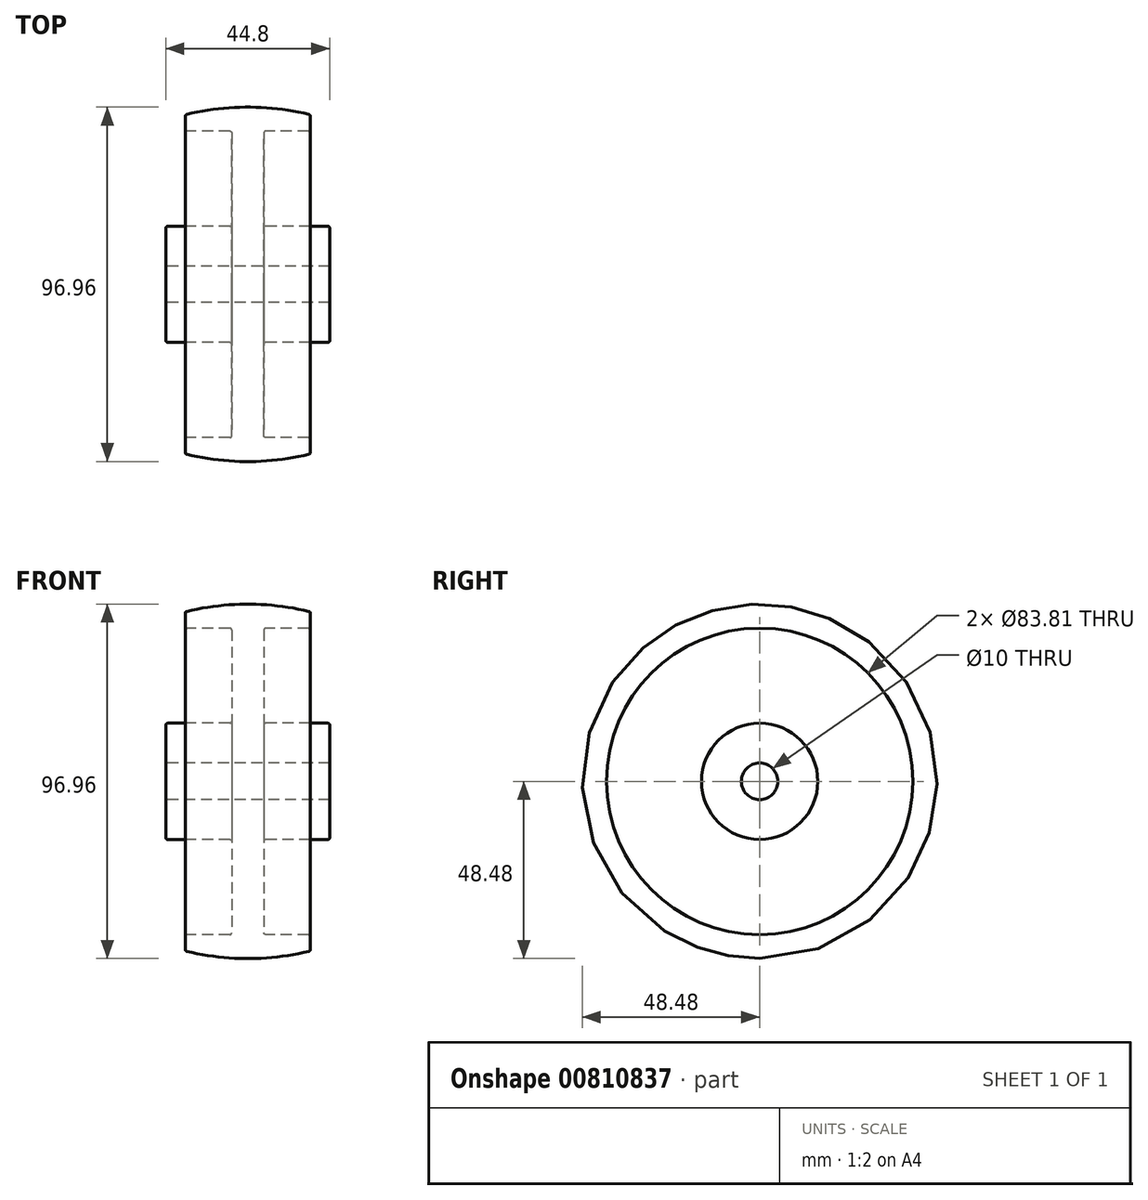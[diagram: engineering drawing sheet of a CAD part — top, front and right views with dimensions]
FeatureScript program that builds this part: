
annotation { "Feature Type Name" : "Feature", "Feature Type Description" : "" }
export const myFeature = defineFeature(function(context is Context, id is Id, definition is map)
    precondition{}
    {
        {
            var Q0;
            Q0=qCreatedBy(makeId("Front.planeOp"),FACE);
            var sketch = newSketch(context, id + "F0", { "sketchPlane" : qUnion([Q0])});
            skLineSegment(sketch, "E0", {"start": v(0, 5) * mm, "end": v(22.4, 5) * mm});
            skLineSegment(sketch, "E1", {"start": v(22.4, 5) * mm, "end": v(22.4, 15.9) * mm});
            skLineSegment(sketch, "E2", {"start": v(22.4, 15.9) * mm, "end": v(4.4, 15.9) * mm});
            skLineSegment(sketch, "E3", {"start": v(4.4, 15.9) * mm, "end": v(4.4, 41.9) * mm});
            skLineSegment(sketch, "E4", {"start": v(4.4, 41.9) * mm, "end": v(17.1, 41.9) * mm});
            skLineSegment(sketch, "E5", {"start": v(17.1, 41.9) * mm, "end": v(17.1, 46.4) * mm});
            skLineSegment(sketch, "E6.MirrorCS", {"start": v(-17.1, 41.9) * mm, "end": v(-17.1, 46.4) * mm});
            skLineSegment(sketch, "E7.MirrorCS", {"start": v(-4.4, 41.9) * mm, "end": v(-17.1, 41.9) * mm});
            skLineSegment(sketch, "E8.MirrorCS", {"start": v(-4.4, 15.9) * mm, "end": v(-4.4, 41.9) * mm});
            skLineSegment(sketch, "E9.MirrorCS", {"start": v(-22.4, 15.9) * mm, "end": v(-4.4, 15.9) * mm});
            skLineSegment(sketch, "E10.MirrorCS", {"start": v(-22.4, 5) * mm, "end": v(-22.4, 15.9) * mm});
            skLineSegment(sketch, "E11.MirrorCS", {"start": v(0, 5) * mm, "end": v(-22.4, 5) * mm});
            skArc(sketch, "E12", {"start": v(17.1, 46.4) * mm, "mid": v(8.6, 47.96) * mm, "end": v(0, 48.48) * mm});
            skArc(sketch, "E13", {"start": v(-17.1, 46.4) * mm, "mid": v(-8.6, 47.96) * mm, "end": v(0, 48.48) * mm});
            skLineSegment(sketch, "E14", {"start": v(-62.65, 0) * mm, "end": v(79.48, 0) * mm});
            skSolve(sketch);
        }
        {
            var Q0;
            Q0=makeQuery(id+"F0.imprint","IMPRINT",FACE,{"disambiguationData":[TD([[makeQuery(id+"F0.imprint","IMPRINT",EDGE,{"derivedFrom":sQuery(id+"F0.wireOp",EDGE,"E0")}),1.0]])]});
            var Q1;
            Q1=sQuery(id+"F0.wireOp",EDGE,"E14");
            revolve(context, id + "F1", {"surfaceOperationType" : NewSurfaceOperationType.NEW, "entities" : qUnion([Q0]), "axis" : qUnion([Q1]), "revolveType" : RevolveType.FULL});
        }
        {
            var Q0;
            Q0=makeQuery(id+"F1.opRevolve","SWEPT_EDGE",EDGE,{"disambiguationData":[OSD([sQuery(id+"F0.wireOp",EDGE,"E6.MirrorCS"),sQuery(id+"F0.wireOp",EDGE,"E13")])]});
            var Q1;
            Q1=makeQuery(id+"F1.opRevolve","SWEPT_EDGE",EDGE,{"disambiguationData":[OSD([sQuery(id+"F0.wireOp",EDGE,"E5"),sQuery(id+"F0.wireOp",EDGE,"E12")])]});
            var Q2;
            Q2=makeQuery(id+"F1.opRevolve","SWEPT_EDGE",EDGE,{"disambiguationData":[OSD([sQuery(id+"F0.wireOp",EDGE,"E6.MirrorCS"),sQuery(id+"F0.wireOp",EDGE,"E7.MirrorCS")])]});
            var Q3;
            Q3=makeQuery(id+"F1.opRevolve","SWEPT_EDGE",EDGE,{"disambiguationData":[OSD([sQuery(id+"F0.wireOp",EDGE,"E4"),sQuery(id+"F0.wireOp",EDGE,"E5")])]});
            var Q4;
            Q4=makeQuery(id+"F1.opRevolve","SWEPT_EDGE",EDGE,{"disambiguationData":[OSD([sQuery(id+"F0.wireOp",EDGE,"E3"),sQuery(id+"F0.wireOp",EDGE,"E4")])]});
            var Q5;
            Q5=makeQuery(id+"F1.opRevolve","SWEPT_EDGE",EDGE,{"disambiguationData":[OSD([sQuery(id+"F0.wireOp",EDGE,"E2"),sQuery(id+"F0.wireOp",EDGE,"E3")])]});
            var Q6;
            Q6=makeQuery(id+"F1.opRevolve","SWEPT_EDGE",EDGE,{"disambiguationData":[OSD([sQuery(id+"F0.wireOp",EDGE,"E7.MirrorCS"),sQuery(id+"F0.wireOp",EDGE,"E8.MirrorCS")])]});
            var Q7;
            Q7=makeQuery(id+"F1.opRevolve","SWEPT_EDGE",EDGE,{"disambiguationData":[OSD([sQuery(id+"F0.wireOp",EDGE,"E8.MirrorCS"),sQuery(id+"F0.wireOp",EDGE,"E9.MirrorCS")])]});
            fillet(context, id + "F2", {"entities" : qUnion([Q0, Q1, Q2, Q3, Q4, Q5, Q6, Q7]), "radius" : 0.5 * mm, "tangentPropagation" : true, "allowEdgeOverflow" : false});
        }
        {
            var Q0;
            Q0=makeQuery(id+"F1.opRevolve","SWEPT_EDGE",EDGE,{"disambiguationData":[OSD([sQuery(id+"F0.wireOp",EDGE,"E1"),sQuery(id+"F0.wireOp",EDGE,"E2")])]});
            var Q1;
            Q1=makeQuery(id+"F1.opRevolve","SWEPT_EDGE",EDGE,{"disambiguationData":[OSD([sQuery(id+"F0.wireOp",EDGE,"E9.MirrorCS"),sQuery(id+"F0.wireOp",EDGE,"E10.MirrorCS")])]});
            fillet(context, id + "F3", {"entities" : qUnion([Q0, Q1]), "radius" : 0.5 * mm, "tangentPropagation" : true, "allowEdgeOverflow" : false});
        }
    });
